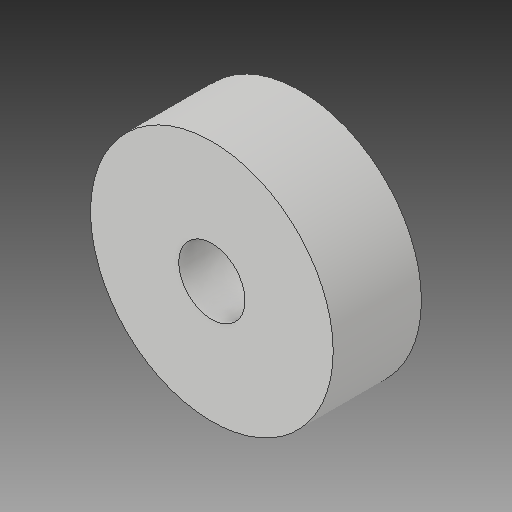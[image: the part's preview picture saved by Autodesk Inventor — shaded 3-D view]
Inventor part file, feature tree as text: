
AUTODESK INVENTOR PART (.ipt)
format: ipt  version: 2017 (Build 210142000, 142)  size: 94,720 bytes
history: native  units: in
note: dims shown in document units (in); Inventor stores cm internally (conversion verified against a paired STEP export)
features: extrude x1, sketch x1
ambient origin geometry x8: Origin, YZ Plane, XZ Plane, XY Plane, X Axis, Y Axis, Z Axis, Center Point
bodies: Solid1 (feature_tree)
feature tree (2):
  extrude  "Extrusion1"  Depth=0.25in
  sketch  "Sketch1"  dims[d0=0.6875in d1=0.1875in d2=0.25in d3=0.0in]
